# Revit family: Graypants_Scraplights_Linear_Drop48_Disc48_Oliv48_Pendants_R21_0925
name_source: partatom
category: Lighting Fixtures
units: mm (PartAtom-declared; Revit-internal decimal feet)

## family parameters
Cut with Voids When Loaded = No
Host = Face
Light Source = Yes
Part Type = Normal
Room Calculation Point = No
Round Connector Dimension = Use Diameter
Shared = No

## types (3) — shared parameters
Color Filter = 16777215
Default Elevation = 4' - 0"
Dimming Lamp Color Temperature Shift = <None>
Emit from Line Length = 2' - 0"
Graypants_Cable_Material_Finish = _Graypants_Steel
Graypants_Cord/Canopy_Finish_Options = White | Black
Graypants_Manufacturer = Graypants
Graypants_Shade_Finish_Options = Natural Cardboard | Blonde Cardboard | White Cardboard
Graypants_URL = https://graypants.com
Light Source Symbol Size = 1' - 6"

## per-type parameters (varying)
| type | Graypants_Disc48_Canopy_Visible | Graypants_Disc48_Cords_Visible | Graypants_Disc48_Hardware_Visible | Graypants_Disc48_Shade_Visible | Graypants_Drop48_Canopy_Visible | Graypants_Drop48_Cords_Visible | Graypants_Drop48_Hardware_Visible | Graypants_Drop48_Shade_Visible | Graypants_Model | Graypants_Oliv48_Canopy_Visible | Graypants_Oliv48_Cords_Visible | Graypants_Oliv48_Hardware_Visible | Graypants_Oliv48_Shade_Visible |
| Graypants_Scraplights_Oliv48_Pendant | No | No | No | No | No | No | No | No | Scraplights_Linear_Oliv48 | Yes | Yes | Yes | Yes |
| Graypants_Scraplights_Drop48_Pendant | No | No | No | No | Yes | Yes | Yes | Yes | Scraplights_Linear_Drop48 | No | No | No | No |
| Graypants_Scraplights_Disc48_Pendant | Yes | Yes | Yes | Yes | No | No | No | No | Scraplights_Linear_Disc48 | No | No | No | No |

## geometry (parser evidence)
native form markers: Sweep x16
no freeform markers — native parametric forms only
